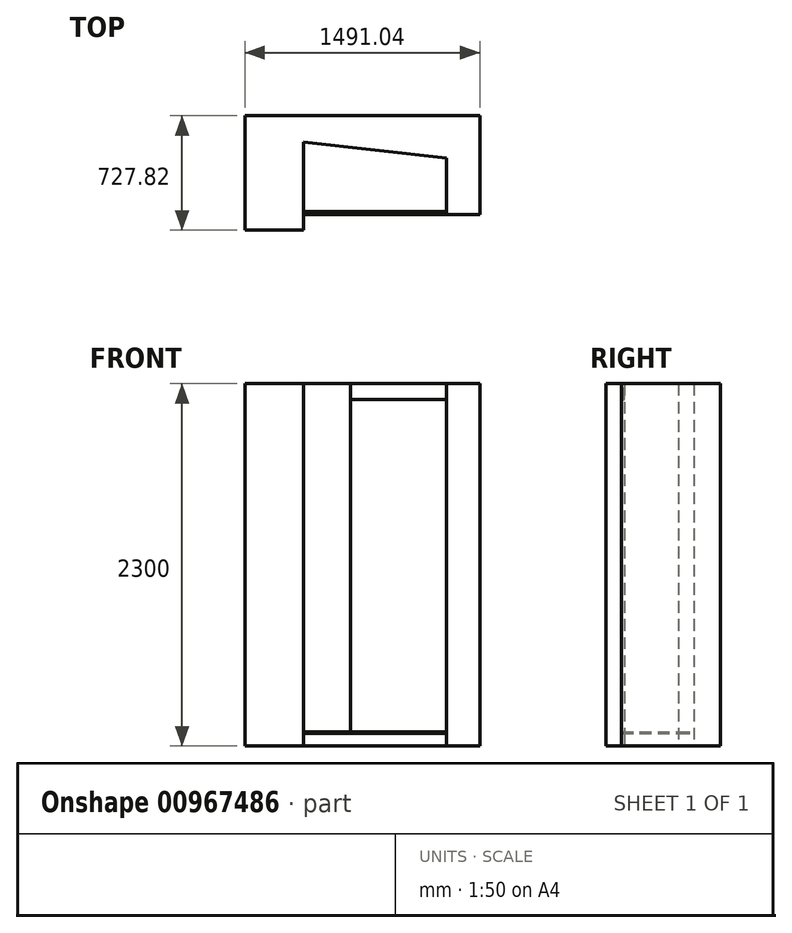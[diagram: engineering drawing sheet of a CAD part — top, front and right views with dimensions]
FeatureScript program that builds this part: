
annotation { "Feature Type Name" : "Feature", "Feature Type Description" : "" }
export const myFeature = defineFeature(function(context is Context, id is Id, definition is map)
    precondition{}
    {
        {
            var Q0;
            Q0=qCreatedBy(makeId("Top.planeOp"),FACE);
            var sketch = newSketch(context, id + "F0", { "sketchPlane" : qUnion([Q0])});
            skLineSegment(sketch, "E0", {"start": v(0, 0) * mm, "end": v(0, 560) * mm});
            skLineSegment(sketch, "E1", {"start": v(0, 560) * mm, "end": v(910, 460) * mm});
            skLineSegment(sketch, "E2", {"start": v(910, 460) * mm, "end": v(910, 100) * mm});
            skLineSegment(sketch, "E3", {"start": v(910, 100) * mm, "end": v(1120.27, 98.57) * mm});
            skLineSegment(sketch, "E4", {"start": v(1120.27, 98.57) * mm, "end": v(1120.27, 727.82) * mm});
            skLineSegment(sketch, "E5", {"start": v(1120.27, 727.82) * mm, "end": v(-370.77, 727.82) * mm});
            skLineSegment(sketch, "E6", {"start": v(-370.77, 727.82) * mm, "end": v(-370.77, 0) * mm});
            skLineSegment(sketch, "E7", {"start": v(-370.77, 0) * mm, "end": v(0, 0) * mm});
            skSolve(sketch);
        }
        {
            var Q0;
            Q0=makeQuery(id+"F0.imprint","IMPRINT",FACE,{"disambiguationData":[TD([[makeQuery(id+"F0.imprint","IMPRINT",EDGE,{"derivedFrom":sQuery(id+"F0.wireOp",EDGE,"E0")}),1.0]])]});
            extrude(context, id + "F1", {"entities" : qUnion([Q0]), "depth" : 2300 * mm, "offsetDistance" : 25 * mm});
        }
        {
            var Q0;
            Q0=qCreatedBy(makeId("Top.planeOp"),FACE);
            var sketch = newSketch(context, id + "F2", { "sketchPlane" : qUnion([Q0])});
            skLineSegment(sketch, "E8.bottom", {"start": v(910, 100) * mm, "end": v(0, 100) * mm});
            skLineSegment(sketch, "E9.top", {"start": v(910, 120) * mm, "end": v(0, 120) * mm});
            skLineSegment(sketch, "E9.left", {"start": v(910, 100) * mm, "end": v(910, 120) * mm});
            skLineSegment(sketch, "E9.right", {"start": v(0, 100) * mm, "end": v(0, 120) * mm});
            skSolve(sketch);
        }
        {
            var Q0;
            Q0=makeQuery(id+"F2.imprint","IMPRINT",FACE,{"disambiguationData":[TD([[makeQuery(id+"F2.imprint","IMPRINT",EDGE,{"derivedFrom":sQuery(id+"F2.wireOp",EDGE,"E8.bottom")}),-1.0]])]});
            extrude(context, id + "F3", {"entities" : qUnion([Q0]), "depth" : 80 * mm, "offsetDistance" : 25 * mm});
        }
        {
            var Q0;
            Q0=makeQuery(id+"F3.opExtrude","CAP_FACE",FACE,{"disambiguationData":[OSD([sQuery(id+"F2.wireOp",EDGE,"E8.bottom"),sQuery(id+"F2.wireOp",EDGE,"E8.top"),sQuery(id+"F2.wireOp",EDGE,"E8.left"),sQuery(id+"F2.wireOp",EDGE,"E8.right")])],"isStart":false});
            var sketch = newSketch(context, id + "F4", { "sketchPlane" : qUnion([Q0])});
            skLineSegment(sketch, "E10.bottom", {"start": v(910, 100) * mm, "end": v(0, 100) * mm});
            skLineSegment(sketch, "E10.top", {"start": v(910, 460) * mm, "end": v(0, 560) * mm});
            skLineSegment(sketch, "E10.left", {"start": v(910, 100) * mm, "end": v(910, 460) * mm});
            skLineSegment(sketch, "E10.right", {"start": v(0, 100) * mm, "end": v(0, 560) * mm});
            skSolve(sketch);
        }
        {
            var Q0;
            Q0 = qSketchRegion(id + "F4", true);
            extrude(context, id + "F5", {"entities" : qUnion([Q0]), "depth" : 10 * mm, "offsetDistance" : 25 * mm});
        }
        {
            var Q0;
            Q0=makeQuery(id+"F5.opExtrude","CAP_FACE",FACE,{"disambiguationData":[OSD([sQuery(id+"F4.wireOp",EDGE,"E10.bottom"),sQuery(id+"F4.wireOp",EDGE,"E10.top"),sQuery(id+"F4.wireOp",EDGE,"E10.left"),sQuery(id+"F4.wireOp",EDGE,"E10.right")])],"isStart":false});
            var sketch = newSketch(context, id + "F6", { "sketchPlane" : qUnion([Q0])});
            skLineSegment(sketch, "E11.bottom", {"start": v(0, 100) * mm, "end": v(300, 100) * mm});
            skLineSegment(sketch, "E11.top", {"start": v(0, 120) * mm, "end": v(300, 120) * mm});
            skLineSegment(sketch, "E11.left", {"start": v(0, 100) * mm, "end": v(0, 120) * mm});
            skLineSegment(sketch, "E11.right", {"start": v(300, 100) * mm, "end": v(300, 120) * mm});
            skSolve(sketch);
        }
        {
            var Q0;
            Q0=makeQuery(id+"F6.imprint","IMPRINT",FACE,{"disambiguationData":[TD([[makeQuery(id+"F6.imprint","IMPRINT",EDGE,{"derivedFrom":sQuery(id+"F6.wireOp",EDGE,"E11.bottom")}),-1.0]])]});
            var Q1;
            Q1=makeQuery(id+"F1.opExtrude","CAP_FACE",FACE,{"disambiguationData":[OSD([sQuery(id+"F0.wireOp",EDGE,"E0"),sQuery(id+"F0.wireOp",EDGE,"E1"),sQuery(id+"F0.wireOp",EDGE,"E2"),sQuery(id+"F0.wireOp",EDGE,"E3"),sQuery(id+"F0.wireOp",EDGE,"E4"),sQuery(id+"F0.wireOp",EDGE,"E5"),sQuery(id+"F0.wireOp",EDGE,"E6"),sQuery(id+"F0.wireOp",EDGE,"E7")])],"isStart":false});
            extrude(context, id + "F7", {"entities" : qUnion([Q0]), "endBound" : BoundingType.UP_TO_SURFACE, "depth" : 25 * mm, "endBoundEntityFace" : qUnion([Q1]), "offsetDistance" : 25 * mm});
        }
        {
            var Q0;
            Q0=makeQuery(id+"F1.opExtrude","CAP_FACE",FACE,{"disambiguationData":[OSD([sQuery(id+"F0.wireOp",EDGE,"E0"),sQuery(id+"F0.wireOp",EDGE,"E1"),sQuery(id+"F0.wireOp",EDGE,"E2"),sQuery(id+"F0.wireOp",EDGE,"E3"),sQuery(id+"F0.wireOp",EDGE,"E4"),sQuery(id+"F0.wireOp",EDGE,"E5"),sQuery(id+"F0.wireOp",EDGE,"E6"),sQuery(id+"F0.wireOp",EDGE,"E7")])],"isStart":false});
            var sketch = newSketch(context, id + "F8", { "sketchPlane" : qUnion([Q0])});
            skLineSegment(sketch, "E12.bottom", {"start": v(300, 100) * mm, "end": v(910, 100) * mm});
            skLineSegment(sketch, "E12.top", {"start": v(300, 120) * mm, "end": v(910, 120) * mm});
            skLineSegment(sketch, "E12.left", {"start": v(300, 100) * mm, "end": v(300, 120) * mm});
            skLineSegment(sketch, "E12.right", {"start": v(910, 100) * mm, "end": v(910, 120) * mm});
            skSolve(sketch);
        }
        {
            var Q0;
            Q0=makeQuery(id+"F8.imprint","IMPRINT",FACE,{"disambiguationData":[TD([[makeQuery(id+"F8.imprint","IMPRINT",EDGE,{"derivedFrom":sQuery(id+"F8.wireOp",EDGE,"E12.bottom")}),1.0]])]});
            extrude(context, id + "F9", {"entities" : qUnion([Q0]), "oppositeDirection" : true, "depth" : 100 * mm, "offsetDistance" : 25 * mm});
        }
    });
